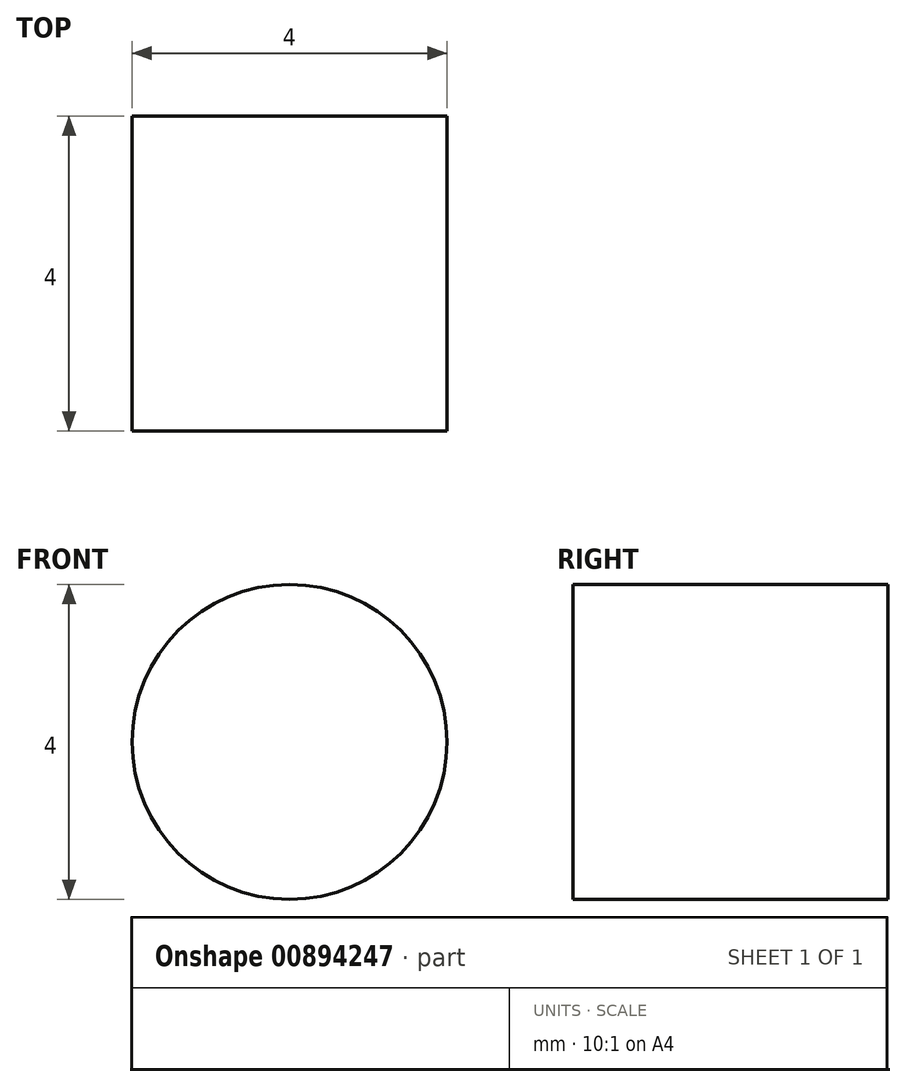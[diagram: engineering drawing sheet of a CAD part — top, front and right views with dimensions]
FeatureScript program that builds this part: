
annotation { "Feature Type Name" : "Feature", "Feature Type Description" : "" }
export const myFeature = defineFeature(function(context is Context, id is Id, definition is map)
    precondition{}
    {
        {
            var Q0;
            Q0=qCreatedBy(makeId("Front.planeOp"),FACE);
            var sketch = newSketch(context, id + "F0", { "sketchPlane" : qUnion([Q0])});
            skCircle(sketch, "E0", {"center": v(0, 0) * mm, "radius": 2 * mm});
            skSolve(sketch);
        }
        {
            var Q0;
            Q0=makeQuery(id+"F0.imprint","IMPRINT",FACE,{"disambiguationData":[TD([[makeQuery(id+"F0.imprint","IMPRINT",EDGE,{"derivedFrom":sQuery(id+"F0.wireOp",EDGE,"E0")}),1.0]])]});
            extrude(context, id + "F1", {"entities" : qUnion([Q0]), "depth" : 4 * mm, "offsetDistance" : 25 * mm});
        }
    });
